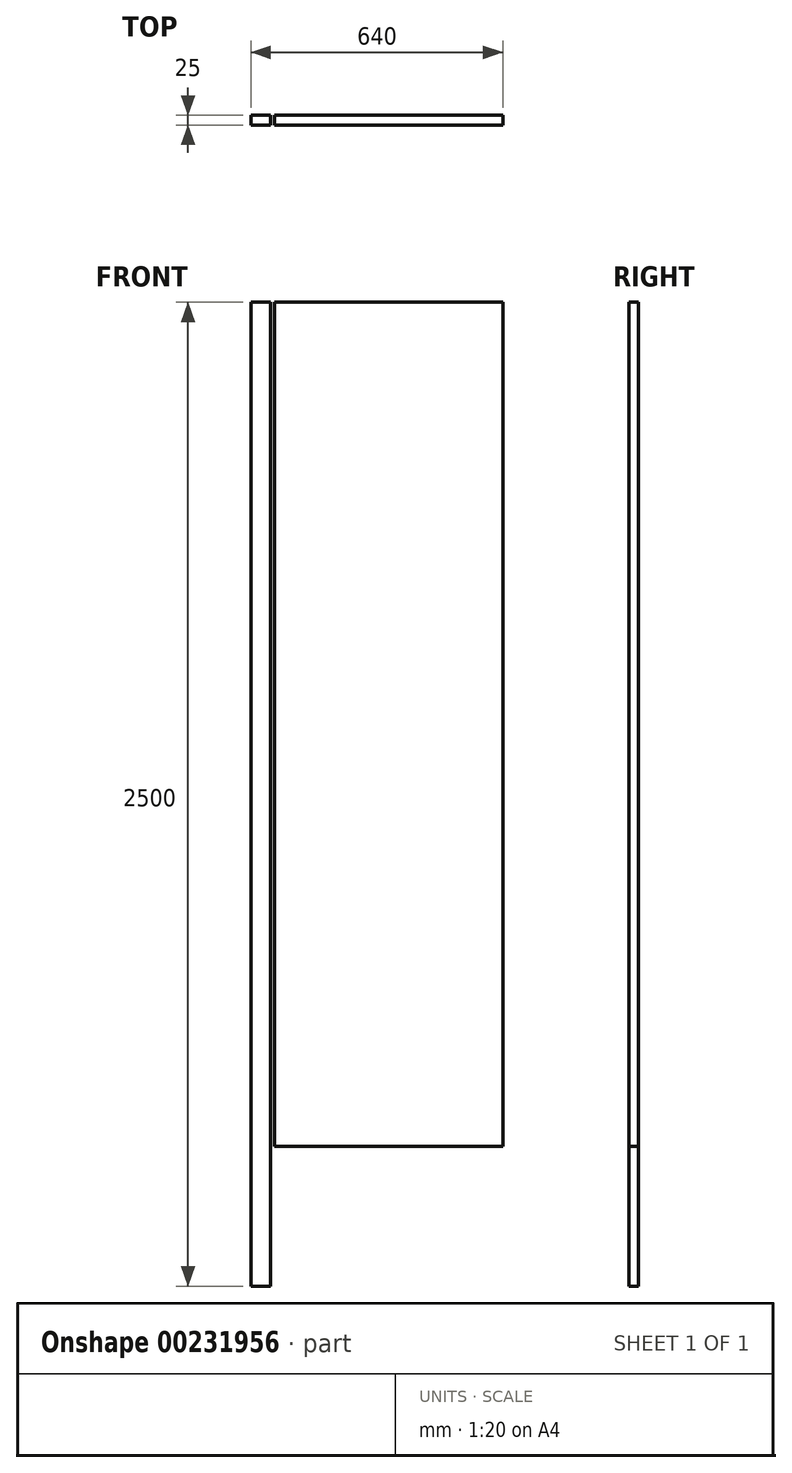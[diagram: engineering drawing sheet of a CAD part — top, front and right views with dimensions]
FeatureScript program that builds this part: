
annotation { "Feature Type Name" : "Feature", "Feature Type Description" : "" }
export const myFeature = defineFeature(function(context is Context, id is Id, definition is map)
    precondition{}
    {
        {
            var Q0;
            Q0=qCreatedBy(makeId("Front.planeOp"),FACE);
            var sketch = newSketch(context, id + "F0", { "sketchPlane" : qUnion([Q0])});
            skLineSegment(sketch, "E0.bottom", {"start": v(-290, 1072.5) * mm, "end": v(290, 1072.5) * mm});
            skLineSegment(sketch, "E0.top", {"start": v(-290, -1072.5) * mm, "end": v(290, -1072.5) * mm});
            skLineSegment(sketch, "E0.left", {"start": v(-290, 1072.5) * mm, "end": v(-290, -1072.5) * mm});
            skLineSegment(sketch, "E0.right", {"start": v(290, 1072.5) * mm, "end": v(290, -1072.5) * mm});
            skPoint(sketch, "E0.middle", {"position": v(0, 0) * mm});
            skSolve(sketch);
        }
        {
            var Q0;
            Q0 = qSketchRegion(id + "F0", true);
            extrude(context, id + "F1", {"entities" : qUnion([Q0]), "depth" : 25 * mm});
        }
        {
            var Q0;
            Q0=qCreatedBy(makeId("Front.planeOp"),FACE);
            var sketch = newSketch(context, id + "F2", { "sketchPlane" : qUnion([Q0])});
            skLineSegment(sketch, "E1.bottom", {"start": v(-300, 1072.5) * mm, "end": v(-350, 1072.5) * mm});
            skLineSegment(sketch, "E1.top", {"start": v(-300, -1427.5) * mm, "end": v(-350, -1427.5) * mm});
            skLineSegment(sketch, "E1.left", {"start": v(-300, 1072.5) * mm, "end": v(-300, -1427.5) * mm});
            skLineSegment(sketch, "E1.right", {"start": v(-350, 1072.5) * mm, "end": v(-350, -1427.5) * mm});
            skSolve(sketch);
        }
        {
            var Q0;
            Q0 = qSketchRegion(id + "F2", true);
            extrude(context, id + "F3", {"entities" : qUnion([Q0]), "depth" : 25 * mm});
        }
    });
